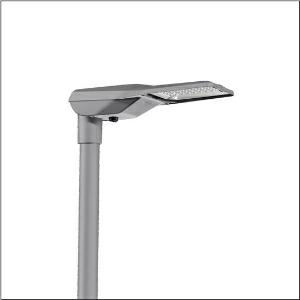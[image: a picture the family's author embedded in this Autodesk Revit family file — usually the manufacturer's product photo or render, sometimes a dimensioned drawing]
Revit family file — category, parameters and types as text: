
# Revit family: streetlight_sl_21_iq_mini___st1_0ab_5xe2m31u08hb_6af5
name_source: partatom
category: Lighting Fixtures
units: mm (PartAtom-declared; Revit-internal decimal feet)

## family parameters
Cut with Voids When Loaded = No
Host = Face
Light Source = No
Part Type = Normal
Room Calculation Point = No
Round Connector Dimension = Use Diameter
Shared = No

## types (1)
- --- (1 x LED, 8580 lm, 71 W, 3000K)
    Apparent Load = 71 VA
    CIE Flux Codes = 38 73 97 100 100
    Color Rendering = 70
    Color Temperature = 3000K
    Default Elevation = 1800 mm
    Description = Streetlight SL 21 iQ mini, mast luminaire, primary light control with lens, of PMMA, primary optical cover: cover, of toughened safety glass, transparent, light distribution: ST1.0aB, light emission: direct distribution, primary light characteristic: asymmetric, installation type: post-top, side-entry, LED, High Power LED, rated luminous flux: 8.580lm, luminous efficacy: 121lm/W, light colour: 730, colour temperature: 3000K, control: presetting dimming logarithmic, Street-Remote, Auto-Match, Temp-Guard, Lumen-Switch, Night-Set, Smart-Wire, Light-Fading, Desk-Remote (wireless, voltage-free reading and setting of iQ features in the workshop via application-optimized NFC function/RFID function), optimised constant luminous flux control (CLO 2.0), mains connection: 220..240V, AC, 50/60Hz, start of lifetime: 71W, end of service life: 75W, reduction: 30W, luminaire housing, of diecast aluminium, powder-coated, Siteco® metallic grey (DB 702S), corrosivity category C5 mid according to DIN EN ISO 12944, please order mast flange separately, inclination adjustable: 0°, 5°, 10°, 15°, sealing non-destructively replaceable, multi-level sealing system, length: 628mm, width: 235mm, height: 110mm, mast flange for spigot size: 42mm (side-entry): 5XC10008XM4, 60/48mm (side-entry/post-top): 5XC10108XM2, 76/60mm (side-entry/post-top): 5XC10108XM1, Smart Interface below, protection rating (complete): IP66, insulation class (complete): insulation class II (safety insulation), certification: CE, ENEC, ENEC+, VDE, impact resistance: IK09, permissible operating ambient temperature for outdoor applications: -40..+50°C, standard-compliant lighting for roads and squares, packaging unit: 1 piece

Light Distribution: ST1.0aB
    Height = 110 mm
    Lamp = 1 x LED
    Lamp Light Flux = 8580 lm
    Lamp Power = 71 W
    Lamp count = 1
    Length = 625 mm
    Luminous efficacy = 121 lm/W
    Manufacturer = Siteco
    ModVariant = No
    Model = 5XE2M31U08HB
    Number of Poles = 1
    OnlyDefault = Yes
    Power Factor = 1
    Product Name = Streetlight SL 21 iQ mini | ST1.0aB
    Product group = mast luminaire | pylon top
    ProductGroupID = 6100
    Protection Class = Protection class II
    Protection Degree = IP 66
    RLX_Detail_Level = 1
    RLX_Emergency_Light_Flux = 0 lm
    RLX_Emergency_Type = 0
    RLX_Emergency_Type_DB = No
    RlxData = <blob elided: 92613 chars, md5=75612046>
    Socket = socket
    Standby Power = 0 W
    System Light Flux = 8580 lm
    System Power = 71 W
    Type Comments = factory setting: luminous flux: 100 % | dim-lin: 254 | 716 mA
    Type Image = l_1003516.jpg
    URL = http://relux.com
    VarID = @adj_042639
    Voltage = 0 V
    Weight = 0.00 kg
    Width = 234 mm

## geometry (parser evidence)
native form markers: Blend x4, Sweep x11
no freeform markers — native parametric forms only
